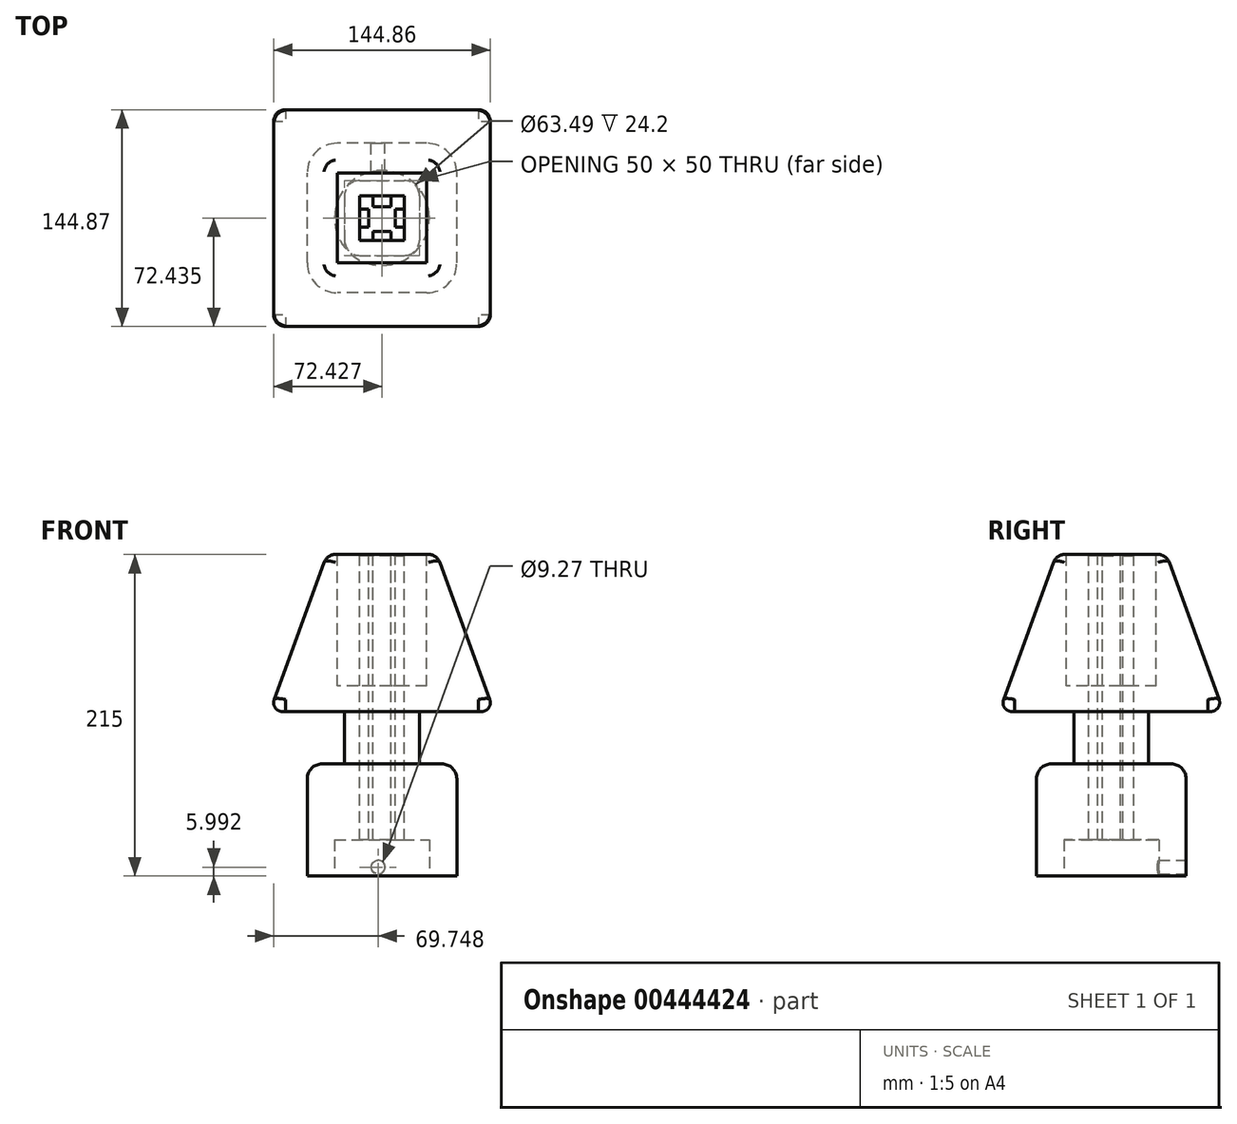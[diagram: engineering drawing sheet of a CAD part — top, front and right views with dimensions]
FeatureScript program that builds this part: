
annotation { "Feature Type Name" : "Feature", "Feature Type Description" : "" }
export const myFeature = defineFeature(function(context is Context, id is Id, definition is map)
    precondition{}
    {
        {
            var Q0;
            Q0=qCreatedBy(makeId("Top.planeOp"),FACE);
            var sketch = newSketch(context, id + "F0", { "sketchPlane" : qUnion([Q0])});
            skLineSegment(sketch, "E0.bottom", {"start": v(5.47, -57.7) * mm, "end": v(-94.53, -57.7) * mm});
            skLineSegment(sketch, "E0.top", {"start": v(5.47, 42.3) * mm, "end": v(-94.53, 42.3) * mm});
            skLineSegment(sketch, "E0.left", {"start": v(5.47, -57.7) * mm, "end": v(5.47, 42.3) * mm});
            skLineSegment(sketch, "E0.right", {"start": v(-94.53, -57.7) * mm, "end": v(-94.53, 42.3) * mm});
            skSolve(sketch);
        }
        {
            var Q0;
            Q0 = qSketchRegion(id + "F0", true);
            extrude(context, id + "F1", {"entities" : qUnion([Q0]), "depth" : 75 * mm});
        }
        {
            var Q0;
            Q0=makeQuery(id+"F1.opExtrude","SWEPT_EDGE",EDGE,{"disambiguationData":[OSD([sQuery(id+"F0.wireOp",EDGE,"E0.bottom"),sQuery(id+"F0.wireOp",EDGE,"E0.left")])]});
            var Q1;
            Q1=makeQuery(id+"F1.opExtrude","SWEPT_EDGE",EDGE,{"disambiguationData":[OSD([sQuery(id+"F0.wireOp",EDGE,"E0.bottom"),sQuery(id+"F0.wireOp",EDGE,"E0.right")])]});
            var Q2;
            Q2=makeQuery(id+"F1.opExtrude","SWEPT_EDGE",EDGE,{"disambiguationData":[OSD([sQuery(id+"F0.wireOp",EDGE,"E0.top"),sQuery(id+"F0.wireOp",EDGE,"E0.left")])]});
            var Q3;
            Q3=makeQuery(id+"F1.opExtrude","SWEPT_EDGE",EDGE,{"disambiguationData":[OSD([sQuery(id+"F0.wireOp",EDGE,"E0.top"),sQuery(id+"F0.wireOp",EDGE,"E0.right")])]});
            fillet(context, id + "F2", {"entities" : qUnion([Q0, Q1, Q2, Q3]), "radius" : 20 * mm, "tangentPropagation" : true, "allowEdgeOverflow" : false});
        }
        {
            var Q0;
            Q0=makeQuery(id+"F1.opExtrude","CAP_FACE",FACE,{"disambiguationData":[OSD([sQuery(id+"F0.wireOp",EDGE,"E0.bottom"),sQuery(id+"F0.wireOp",EDGE,"E0.top"),sQuery(id+"F0.wireOp",EDGE,"E0.left"),sQuery(id+"F0.wireOp",EDGE,"E0.right")])],"isStart":false});
            var sketch = newSketch(context, id + "F3", { "sketchPlane" : qUnion([Q0])});
            skLineSegment(sketch, "E1.bottom", {"start": v(-69.53, 17.3) * mm, "end": v(-19.53, 17.3) * mm});
            skLineSegment(sketch, "E1.top", {"start": v(-69.53, -32.7) * mm, "end": v(-19.53, -32.7) * mm});
            skLineSegment(sketch, "E1.left", {"start": v(-69.53, 17.3) * mm, "end": v(-69.53, -32.7) * mm});
            skLineSegment(sketch, "E1.right", {"start": v(-19.53, 17.3) * mm, "end": v(-19.53, -32.7) * mm});
            skSolve(sketch);
        }
        {
            var Q0;
            Q0 = qSketchRegion(id + "F3", true);
            extrude(context, id + "F4", {"entities" : qUnion([Q0]), "operationType" : NewBodyOperationType.ADD, "depth" : 35 * mm});
        }
        {
            var Q0;
            Q0=makeQuery(id+"F4.opExtrude","SWEPT_EDGE",EDGE,{"disambiguationData":[OSD([sQuery(id+"F3.wireOp",EDGE,"E1.top"),sQuery(id+"F3.wireOp",EDGE,"E1.right")])]});
            var Q1;
            Q1=makeQuery(id+"F4.opExtrude","SWEPT_EDGE",EDGE,{"disambiguationData":[OSD([sQuery(id+"F3.wireOp",EDGE,"E1.top"),sQuery(id+"F3.wireOp",EDGE,"E1.left")])]});
            var Q2;
            Q2=makeQuery(id+"F4.opExtrude","SWEPT_EDGE",EDGE,{"disambiguationData":[OSD([sQuery(id+"F3.wireOp",EDGE,"E1.bottom"),sQuery(id+"F3.wireOp",EDGE,"E1.right")])]});
            var Q3;
            Q3=makeQuery(id+"F4.opExtrude","SWEPT_EDGE",EDGE,{"disambiguationData":[OSD([sQuery(id+"F3.wireOp",EDGE,"E1.bottom"),sQuery(id+"F3.wireOp",EDGE,"E1.left")])]});
            fillet(context, id + "F5", {"entities" : qUnion([Q0, Q1, Q2, Q3]), "radius" : 10 * mm, "tangentPropagation" : true, "allowEdgeOverflow" : false});
        }
        {
            var Q0;
            Q0=makeQuery(id+"F4.opExtrude","CAP_FACE",FACE,{"disambiguationData":[OSD([sQuery(id+"F3.wireOp",EDGE,"E1.bottom"),sQuery(id+"F3.wireOp",EDGE,"E1.top"),sQuery(id+"F3.wireOp",EDGE,"E1.left"),sQuery(id+"F3.wireOp",EDGE,"E1.right")])],"isStart":false});
            var sketch = newSketch(context, id + "F6", { "sketchPlane" : qUnion([Q0])});
            skLineSegment(sketch, "E2.bottom", {"start": v(-119.53, 67.3) * mm, "end": v(30.47, 67.3) * mm});
            skLineSegment(sketch, "E2.top", {"start": v(-119.53, -82.7) * mm, "end": v(30.47, -82.7) * mm});
            skLineSegment(sketch, "E2.left", {"start": v(-119.53, 67.3) * mm, "end": v(-119.53, -82.7) * mm});
            skLineSegment(sketch, "E2.right", {"start": v(30.47, 67.3) * mm, "end": v(30.47, -82.7) * mm});
            skSolve(sketch);
        }
        {
            var Q0;
            Q0 = qSketchRegion(id + "F6", true);
            extrude(context, id + "F7", {"entities" : qUnion([Q0]), "operationType" : NewBodyOperationType.ADD, "depth" : 105 * mm, "hasDraft" : true, "draftAngle" : 20 * degree, "draftPullDirection" : true});
        }
        {
            var Q0;
            Q0=makeQuery(id+"F7.opExtrude","CAP_EDGE",EDGE,{"disambiguationData":[OSD([sQuery(id+"F6.wireOp",EDGE,"E2.left")])],"isStart":false});
            var Q1;
            Q1=makeQuery(id+"F7.opExtrude","SWEPT_EDGE",EDGE,{"disambiguationData":[OSD([sQuery(id+"F6.wireOp",EDGE,"E2.top"),sQuery(id+"F6.wireOp",EDGE,"E2.left")])]});
            var Q2;
            Q2=makeQuery(id+"F7.opExtrude","CAP_EDGE",EDGE,{"disambiguationData":[OSD([sQuery(id+"F6.wireOp",EDGE,"E2.top")])],"isStart":false});
            var Q3;
            Q3=makeQuery(id+"F7.opExtrude","CAP_EDGE",EDGE,{"disambiguationData":[OSD([sQuery(id+"F6.wireOp",EDGE,"E2.right")])],"isStart":false});
            var Q4;
            Q4=makeQuery(id+"F7.opExtrude","SWEPT_EDGE",EDGE,{"disambiguationData":[OSD([sQuery(id+"F6.wireOp",EDGE,"E2.top"),sQuery(id+"F6.wireOp",EDGE,"E2.right")])]});
            var Q5;
            Q5=makeQuery(id+"F7.opExtrude","SWEPT_EDGE",EDGE,{"disambiguationData":[OSD([sQuery(id+"F6.wireOp",EDGE,"E2.bottom"),sQuery(id+"F6.wireOp",EDGE,"E2.right")])]});
            var Q6;
            Q6=makeQuery(id+"F7.opExtrude","CAP_EDGE",EDGE,{"disambiguationData":[OSD([sQuery(id+"F6.wireOp",EDGE,"E2.bottom")])],"isStart":false});
            var Q7;
            Q7=makeQuery(id+"F7.opExtrude","SWEPT_EDGE",EDGE,{"disambiguationData":[OSD([sQuery(id+"F6.wireOp",EDGE,"E2.bottom"),sQuery(id+"F6.wireOp",EDGE,"E2.left")])]});
            fillet(context, id + "F8", {"entities" : qUnion([Q0, Q1, Q2, Q3, Q4, Q5, Q6, Q7]), "radius" : 8 * mm, "tangentPropagation" : true, "allowEdgeOverflow" : false});
        }
        {
            var Q0;
            Q0=makeQuery(id+"F7.opExtrude","CAP_EDGE",EDGE,{"disambiguationData":[OSD([sQuery(id+"F6.wireOp",EDGE,"E2.top")])],"isStart":true});
            var Q1;
            Q1=makeQuery(id+"F7.opExtrude","CAP_EDGE",EDGE,{"disambiguationData":[OSD([sQuery(id+"F6.wireOp",EDGE,"E2.left")])],"isStart":true});
            var Q2;
            Q2=makeQuery(id+"F7.opExtrude","CAP_EDGE",EDGE,{"disambiguationData":[OSD([sQuery(id+"F6.wireOp",EDGE,"E2.right")])],"isStart":true});
            var Q3;
            Q3=makeQuery(id+"F7.opExtrude","CAP_EDGE",EDGE,{"disambiguationData":[OSD([sQuery(id+"F6.wireOp",EDGE,"E2.bottom")])],"isStart":true});
            fillet(context, id + "F9", {"entities" : qUnion([Q0, Q1, Q2, Q3]), "radius" : 6 * mm, "tangentPropagation" : true, "allowEdgeOverflow" : false});
        }
        {
            var Q0;
            Q0=makeQuery(id+"F1.opExtrude","CAP_EDGE",EDGE,{"disambiguationData":[OSD([sQuery(id+"F0.wireOp",EDGE,"E0.bottom")])],"isStart":false});
            fillet(context, id + "F10", {"entities" : qUnion([Q0]), "radius" : 10 * mm, "tangentPropagation" : true, "allowEdgeOverflow" : false});
        }
        {
            var Q0;
            Q0=makeQuery(id+"F0.imprint","IMPRINT",FACE,{"disambiguationData":[TD([[makeQuery(id+"F0.imprint","IMPRINT",EDGE,{"derivedFrom":sQuery(id+"F0.wireOp",EDGE,"E0.bottom")}),-1.0]])]});
            var sketch = newSketch(context, id + "F11", { "sketchPlane" : qUnion([Q0])});
            skLineSegment(sketch, "E3.bottom", {"start": v(8.38, -10.6) * mm, "end": v(-37.38, -10.6) * mm});
            skLineSegment(sketch, "E3.top", {"start": v(8.38, 0) * mm, "end": v(-37.38, 0) * mm});
            skLineSegment(sketch, "E3.left", {"start": v(8.38, -10.6) * mm, "end": v(8.38, 0) * mm});
            skLineSegment(sketch, "E3.right", {"start": v(-37.38, -10.6) * mm, "end": v(-37.38, 0) * mm});
            skSolve(sketch);
        }
        {
            var Q0;
            {var subQ0=sQuery(id+"F11.wireOp",EDGE,"E3.left");Q0=makeQuery(id+"F11.imprint","IMPRINT",FACE,{"disambiguationData":[TD([[makeQuery(id+"F11.imprint","IMPRINT",EDGE,{"derivedFrom":subQ0}),1.0]])]});}
            extrude(context, id + "F12", {"entities" : qUnion([Q0]), "operationType" : NewBodyOperationType.REMOVE, "oppositeDirection" : true, "depth" : 5 * mm});
        }
        {
            var Q0;
            Q0=makeQuery(id+"F7.opExtrude","CAP_FACE",FACE,{"disambiguationData":[OSD([sQuery(id+"F6.wireOp",EDGE,"E2.bottom"),sQuery(id+"F6.wireOp",EDGE,"E2.top"),sQuery(id+"F6.wireOp",EDGE,"E2.left"),sQuery(id+"F6.wireOp",EDGE,"E2.right")])],"isStart":false});
            var sketch = newSketch(context, id + "F13", { "sketchPlane" : qUnion([Q0])});
            skLineSegment(sketch, "E4.bottom", {"start": v(-14.53, 22.3) * mm, "end": v(-74.53, 22.3) * mm});
            skLineSegment(sketch, "E4.top", {"start": v(-14.53, -37.7) * mm, "end": v(-74.53, -37.7) * mm});
            skLineSegment(sketch, "E4.left", {"start": v(-14.53, 22.3) * mm, "end": v(-14.53, -37.7) * mm});
            skLineSegment(sketch, "E4.right", {"start": v(-74.53, 22.3) * mm, "end": v(-74.53, -37.7) * mm});
            skPoint(sketch, "E4.middle", {"position": v(-44.53, -7.7) * mm});
            skPoint(sketch, "E4.middle.positionSnap0", {"position": v(-44.53, -38.88) * mm});
            skPoint(sketch, "E4.middle.positionSnap1", {"position": v(-75.71, -7.7) * mm});
            skPoint(sketch, "E4.centerSnap0", {"position": v(-44.53, -38.88) * mm});
            skPoint(sketch, "E4.centerSnap1", {"position": v(-75.71, -7.7) * mm});
            skSolve(sketch);
        }
        {
            var Q0;
            Q0 = qSketchRegion(id + "F13", true);
            extrude(context, id + "F14", {"entities" : qUnion([Q0]), "operationType" : NewBodyOperationType.REMOVE, "oppositeDirection" : true, "depth" : 88 * mm, "offsetDistance" : 25 * mm});
        }
        {
            var Q0;
            Q0=makeQuery(id+"F14.boolean.opBoolean","COPY",FACE,{"derivedFrom":makeQuery(id+"F14.opExtrude","CAP_FACE",FACE,{"disambiguationData":[OSD([sQuery(id+"F13.wireOp",EDGE,"E4.bottom"),sQuery(id+"F13.wireOp",EDGE,"E4.top"),sQuery(id+"F13.wireOp",EDGE,"E4.left"),sQuery(id+"F13.wireOp",EDGE,"E4.right")])],"isStart":false})});
            var sketch = newSketch(context, id + "F15", { "sketchPlane" : qUnion([Q0])});
            skLineSegment(sketch, "E5.bottom", {"start": v(-29.53, 7.3) * mm, "end": v(-59.53, 7.3) * mm});
            skLineSegment(sketch, "E5.top", {"start": v(-29.53, -22.7) * mm, "end": v(-59.53, -22.7) * mm});
            skLineSegment(sketch, "E5.left", {"start": v(-29.53, 7.3) * mm, "end": v(-29.53, -22.7) * mm});
            skLineSegment(sketch, "E5.right", {"start": v(-59.53, 7.3) * mm, "end": v(-59.53, -22.7) * mm});
            skPoint(sketch, "E5.middle", {"position": v(-44.53, -7.7) * mm});
            skPoint(sketch, "E5.middle.positionSnap0", {"position": v(-44.53, 22.3) * mm});
            skPoint(sketch, "E5.middle.positionSnap1", {"position": v(-74.53, -7.7) * mm});
            skPoint(sketch, "E5.centerSnap0", {"position": v(-44.53, 22.3) * mm});
            skPoint(sketch, "E5.centerSnap1", {"position": v(-74.53, -7.7) * mm});
            skSolve(sketch);
        }
        {
            var Q0;
            Q0 = qSketchRegion(id + "F15", true);
            extrude(context, id + "F16", {"entities" : qUnion([Q0]), "operationType" : NewBodyOperationType.ADD, "depth" : 87.1 * mm, "offsetDistance" : 25 * mm});
        }
        {
            var Q0;
            Q0=makeQuery(id+"F16.opExtrude","CAP_FACE",FACE,{"disambiguationData":[OSD([sQuery(id+"F15.wireOp",EDGE,"E5.bottom"),sQuery(id+"F15.wireOp",EDGE,"E5.top"),sQuery(id+"F15.wireOp",EDGE,"E5.left"),sQuery(id+"F15.wireOp",EDGE,"E5.right")])],"isStart":false});
            var sketch = newSketch(context, id + "F17", { "sketchPlane" : qUnion([Q0])});
            skLineSegment(sketch, "E6.bottom", {"start": v(-53.53, -13.7) * mm, "end": v(-65.53, -13.7) * mm});
            skLineSegment(sketch, "E6.top", {"start": v(-53.53, -1.7) * mm, "end": v(-65.53, -1.7) * mm});
            skLineSegment(sketch, "E6.left", {"start": v(-53.53, -13.7) * mm, "end": v(-53.53, -1.7) * mm});
            skLineSegment(sketch, "E6.right", {"start": v(-65.53, -13.7) * mm, "end": v(-65.53, -1.7) * mm});
            skPoint(sketch, "E6.middle", {"position": v(-59.53, -7.7) * mm});
            skPoint(sketch, "E7.middle", {"position": v(-44.53, 7.3) * mm});
            skLineSegment(sketch, "E8.bottom", {"start": v(-50.53, -16.7) * mm, "end": v(-38.53, -16.7) * mm});
            skLineSegment(sketch, "E8.top", {"start": v(-50.53, -28.7) * mm, "end": v(-38.53, -28.7) * mm});
            skLineSegment(sketch, "E8.left", {"start": v(-50.53, -16.7) * mm, "end": v(-50.53, -28.7) * mm});
            skLineSegment(sketch, "E8.right", {"start": v(-38.53, -16.7) * mm, "end": v(-38.53, -28.7) * mm});
            skPoint(sketch, "E8.middle", {"position": v(-44.53, -22.7) * mm});
            skPoint(sketch, "E9.middle", {"position": v(-29.53, -7.7) * mm});
            skLineSegment(sketch, "E10.bottom", {"start": v(-35.53, -13.7) * mm, "end": v(-23.53, -13.7) * mm});
            skLineSegment(sketch, "E10.top", {"start": v(-35.53, -1.7) * mm, "end": v(-23.53, -1.7) * mm});
            skLineSegment(sketch, "E10.left", {"start": v(-35.53, -13.7) * mm, "end": v(-35.53, -1.7) * mm});
            skLineSegment(sketch, "E10.right", {"start": v(-23.53, -13.7) * mm, "end": v(-23.53, -1.7) * mm});
            skLineSegment(sketch, "E11.bottom", {"start": v(-38.53, 0) * mm, "end": v(-50.53, 0) * mm});
            skLineSegment(sketch, "E11.top", {"start": v(-38.53, 14.6) * mm, "end": v(-50.53, 14.6) * mm});
            skLineSegment(sketch, "E11.left", {"start": v(-38.53, 0) * mm, "end": v(-38.53, 14.6) * mm});
            skLineSegment(sketch, "E11.right", {"start": v(-50.53, 0) * mm, "end": v(-50.53, 14.6) * mm});
            skSolve(sketch);
        }
        {
            var Q0;
            {var subQ0=sQuery(id+"F17.wireOp",EDGE,"E8.bottom");Q0=makeQuery(id+"F17.imprint","IMPRINT",FACE,{"disambiguationData":[TD([[makeQuery(id+"F17.imprint","IMPRINT",EDGE,{"derivedFrom":subQ0}),-1.0]])]});}
            var Q1;
            {var subQ0=sQuery(id+"F17.wireOp",EDGE,"E6.left");Q1=makeQuery(id+"F17.imprint","IMPRINT",FACE,{"disambiguationData":[TD([[makeQuery(id+"F17.imprint","IMPRINT",EDGE,{"derivedFrom":subQ0}),1.0]])]});}
            var Q2;
            {var subQ0=sQuery(id+"F17.wireOp",EDGE,"E11.bottom");Q2=makeQuery(id+"F17.imprint","IMPRINT",FACE,{"disambiguationData":[TD([[makeQuery(id+"F17.imprint","IMPRINT",EDGE,{"derivedFrom":subQ0}),-1.0]])]});}
            var Q3;
            {var subQ0=sQuery(id+"F17.wireOp",EDGE,"E10.left");Q3=makeQuery(id+"F17.imprint","IMPRINT",FACE,{"disambiguationData":[TD([[makeQuery(id+"F17.imprint","IMPRINT",EDGE,{"derivedFrom":subQ0}),-1.0]])]});}
            extrude(context, id + "F18", {"entities" : qUnion([Q0, Q1, Q2, Q3]), "operationType" : NewBodyOperationType.REMOVE, "oppositeDirection" : true, "depth" : 281.8 * mm, "offsetDistance" : 25 * mm});
        }
        {
            var Q0;
            Q0=makeQuery(id+"F1.opExtrude","CAP_FACE",FACE,{"disambiguationData":[OSD([sQuery(id+"F0.wireOp",EDGE,"E0.bottom"),sQuery(id+"F0.wireOp",EDGE,"E0.top"),sQuery(id+"F0.wireOp",EDGE,"E0.left"),sQuery(id+"F0.wireOp",EDGE,"E0.right")])],"isStart":true});
            var sketch = newSketch(context, id + "F19", { "sketchPlane" : qUnion([Q0])});
            skSolve(sketch);
        }
        {
            var Q0;
            {var subQ3=sQuery(id+"F0.wireOp",EDGE,"E0.bottom");Q0=makeQuery(id+"F19.imprint","IMPRINT",FACE,{"disambiguationData":[TD([[makeQuery(id+"F19.imprint","IMPRINT",EDGE,{"derivedFrom":makeQuery(id+"F1.opExtrude","CAP_EDGE",EDGE,{"disambiguationData":[OSD([subQ3])],"isStart":true})}),1.0]])]});}
            var sketch = newSketch(context, id + "F20", { "sketchPlane" : qUnion([Q0])});
            skLineSegment(sketch, "E12.0.0", {"start": v(-74.53, -42.3) * mm, "end": v(-14.53, -42.3) * mm});
            skArc(sketch, "E12.0.1", {"start": v(-14.53, -42.3) * mm, "mid": v(-0.4, -36.45) * mm, "end": v(5.47, -22.3) * mm});
            skLineSegment(sketch, "E12.0.2", {"start": v(5.47, -22.3) * mm, "end": v(5.47, 37.7) * mm});
            skArc(sketch, "E12.0.3", {"start": v(5.47, 37.7) * mm, "mid": v(-0.4, 51.84) * mm, "end": v(-14.53, 57.7) * mm});
            skLineSegment(sketch, "E12.0.4", {"start": v(-14.53, 57.7) * mm, "end": v(-74.53, 57.7) * mm});
            skArc(sketch, "E12.0.5", {"start": v(-74.53, 57.7) * mm, "mid": v(-88.67, 51.84) * mm, "end": v(-94.53, 37.7) * mm});
            skLineSegment(sketch, "E12.0.6", {"start": v(-94.53, 37.7) * mm, "end": v(-94.53, -22.3) * mm});
            skArc(sketch, "E12.0.7", {"start": v(-94.53, -22.3) * mm, "mid": v(-88.67, -36.45) * mm, "end": v(-74.53, -42.3) * mm});
            skCircle(sketch, "E13", {"center": v(-44.53, 7.7) * mm, "radius": 31.74 * mm});
            skPoint(sketch, "E13.centerSnap0", {"position": v(-44.53, -42.3) * mm});
            skPoint(sketch, "E13.centerSnap1", {"position": v(-94.53, 7.7) * mm});
            skSolve(sketch);
        }
        {
            var Q0;
            Q0=makeQuery(id+"F20.imprint","IMPRINT",FACE,{"disambiguationData":[TD([[makeQuery(id+"F20.imprint","IMPRINT",EDGE,{"derivedFrom":sQuery(id+"F20.wireOp",EDGE,"E13")}),1.0]])]});
            extrude(context, id + "F21", {"entities" : qUnion([Q0]), "operationType" : NewBodyOperationType.REMOVE, "oppositeDirection" : true, "depth" : 24.2 * mm, "offsetDistance" : 25 * mm});
        }
        {
            var Q0;
            Q0=makeQuery(id+"F1.opExtrude","SWEPT_FACE",FACE,{"disambiguationData":[OSD([sQuery(id+"F0.wireOp",EDGE,"E0.top")])]});
            var sketch = newSketch(context, id + "F22", { "sketchPlane" : qUnion([Q0])});
            skLineSegment(sketch, "E14.0.0", {"start": v(74.53, 0) * mm, "end": v(74.53, 65) * mm});
            skLineSegment(sketch, "E14.0.1", {"start": v(74.53, 65) * mm, "end": v(14.53, 65) * mm});
            skLineSegment(sketch, "E14.0.2", {"start": v(14.53, 65) * mm, "end": v(14.53, 0) * mm});
            skLineSegment(sketch, "E14.0.3", {"start": v(14.53, 0) * mm, "end": v(74.53, 0) * mm});
            skCircle(sketch, "E15", {"center": v(47.21, 6) * mm, "radius": 4.63 * mm});
            skSolve(sketch);
        }
        {
            var Q0;
            Q0=makeQuery(id+"F22.imprint","IMPRINT",FACE,{"disambiguationData":[TD([[makeQuery(id+"F22.imprint","IMPRINT",EDGE,{"derivedFrom":sQuery(id+"F22.wireOp",EDGE,"E15")}),1.0]])]});
            extrude(context, id + "F23", {"entities" : qUnion([Q0]), "operationType" : NewBodyOperationType.REMOVE, "oppositeDirection" : true, "depth" : 25 * mm, "offsetDistance" : 25 * mm});
        }
    });
